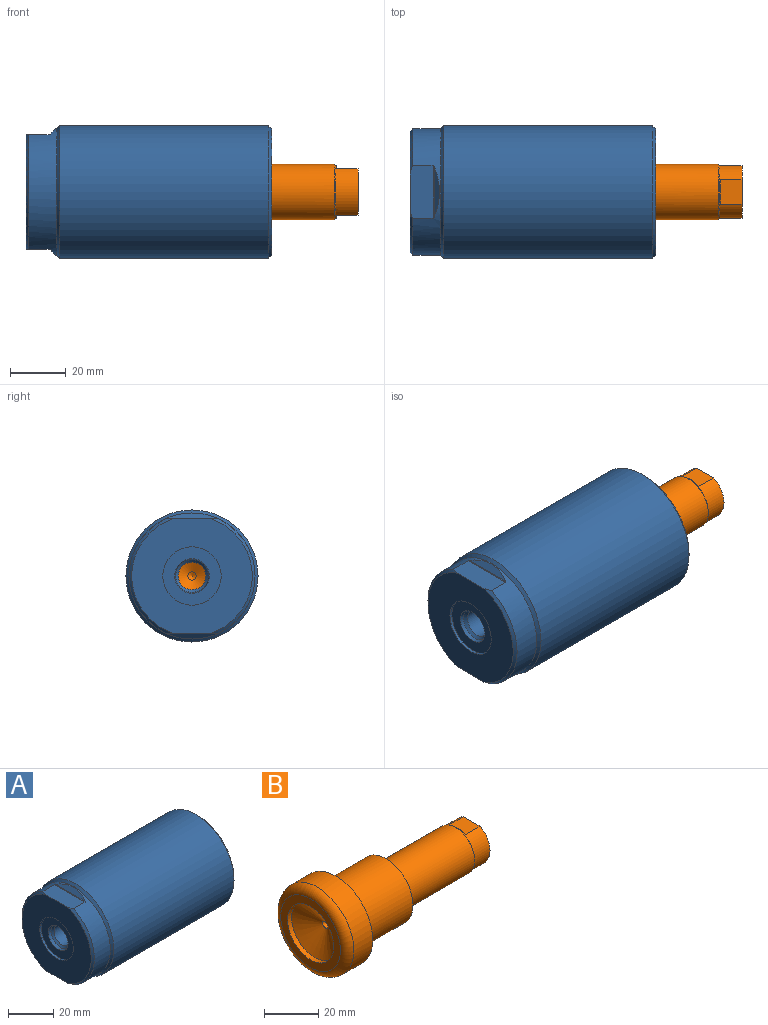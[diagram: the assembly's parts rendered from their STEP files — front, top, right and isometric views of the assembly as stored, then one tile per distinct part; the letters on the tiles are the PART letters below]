
ASSEMBLY  parts=2 mates=1
PART A: 32 faces, bbox 88.6x47.7x47.7 mm
  f0: cone r=0mm half-angle=45deg, axis (1,0,0), area 46mm2, adj f1,f2
  f1: plane 19.8x19.8mm, normal (1,0,0), area 198.7mm2, adj f0,f3
  f2: cylinder r=4.94mm len=9.88mm, axis (1,0,0), area 258.5mm2, adj f0,f4
  f3: cone r=0mm half-angle=45deg, axis (-1,0,0), area 152.1mm2, adj f1,f5
  f4: cone r=0mm half-angle=45deg, axis (-1,0,0), area 46mm2, adj f2,f6
  f5: plane 32.13x32.13mm, normal (1,0,0), area 395.3mm2, adj f3,f7
  f6: cone r=0mm half-angle=12deg, axis (-1,0,0), area 52.9mm2, adj f4,f8
  f7: torus R=16.06mm, axis (1,0,0), area 532.2mm2, adj f5,f9
  f8: plane 21.03x21.03mm, normal (-1,0,0), area 227.2mm2, adj f6,f10
  f9: cylinder r=19.06mm len=60.4mm, axis (1,0,0), area 7235.3mm2, adj f7,f11
  f10: cylinder r=10.52mm len=21.03mm, axis (1,0,0), area 66.1mm2, adj f8,f12
  f11: cone r=0mm half-angle=15deg, axis (1,0,0), area 315.5mm2, adj f9,f13
  f12: plane 43.4x41.2mm, normal (-1,0,0), area 1111.8mm2, adj f10,f15,f19,f20,f21
  f13: plane 40.1x40.1mm, normal (1,0,0), area 39.4mm2, adj f11,f22
  f14: plane 18.43x1.95mm, normal (-0.71,0,-0.71), area 34.2mm2, adj f16,f23
  f15: plane 19.19x8.41mm, normal (0,0,-1), area 155.6mm2, adj f12,f16,f20,f21,f23
  f16: cylinder r=0.5mm len=19.07mm, axis (0,-1,0), area 7.4mm2, adj f14,f15,f23
  f17: plane 18.43x1.95mm, normal (-0.71,0,0.71), area 34.2mm2, adj f18,f23
  f18: cylinder r=0.5mm len=19.07mm, axis (0,-1,0), area 7.4mm2, adj f17,f19,f23
  f19: plane 19.19x8.41mm, normal (0,0,1), area 155.6mm2, adj f12,f18,f20,f21,f23
  f20: cone r=0mm half-angle=45deg, axis (1,0,0), area 75mm2, adj f12,f15,f19,f23
  f21: cone r=0mm half-angle=45deg, axis (1,0,0), area 75mm2, adj f12,f15,f19,f23
  f22: torus R=20.05mm, axis (1,0,0), area 204.2mm2, adj f13,f24
  f23: cylinder r=22.7mm len=45.4mm, axis (-1,0,0), area 1076.3mm2, adj f14,f15,f16,f17,f18,f19,f20,f21
  f24: cylinder r=21.05mm len=42.1mm, axis (1,0,0), area 132.3mm2, adj f22,f26
  f25: cone r=0mm half-angle=45deg, axis (1,0,0), area 225.1mm2, adj f23,f27
  f26: cone r=0mm half-angle=45deg, axis (-1,0,0), area 157.9mm2, adj f24,f28
  f27: cylinder r=23.79mm len=75.41mm, axis (-1,0,0), area 11272.1mm2, adj f25,f29
  f28: cylinder r=20.19mm len=40.38mm, axis (-1,0,0), area 999mm2, adj f26,f30
  f29: cone r=0mm half-angle=45deg, axis (-1,0,0), area 206.9mm2, adj f27,f31
  f30: cone r=0mm half-angle=45deg, axis (1,0,0), area 157.9mm2, adj f28,f31
  f31: plane 45.58x45.58mm, normal (1,0,0), area 239.6mm2, adj f29,f30
PART B: 22 faces, bbox 83.8x41.2x41.2 mm
  f0: cone r=0mm half-angle=62deg, axis (-1,0,0), area 8mm2, adj f1
  f1: cylinder r=1.5mm len=3mm, axis (1,0,0), area 28.3mm2, adj f0,f2
  f2: cone r=0mm half-angle=62deg, axis (-1,0,0), area 504.4mm2, adj f1,f3
  f3: cylinder r=12mm len=24mm, axis (1,0,0), area 158.3mm2, adj f2,f4
  f4: plane 31.02x31.02mm, normal (-1,0,0), area 303.3mm2, adj f3,f5
  f5: torus R=15.51mm, axis (1,0,0), area 612.7mm2, adj f4,f6
  f6: cylinder r=19.01mm len=38.02mm, axis (1,0,0), area 1170.5mm2, adj f5,f7
  f7: plane 38.02x38.02mm, normal (1,0,0), area 479.3mm2, adj f6,f8
  f8: torus R=14.45mm, axis (1,0,0), area 69.7mm2, adj f7,f9
  f9: cylinder r=13.95mm len=27.9mm, axis (1,0,0), area 2235.1mm2, adj f8,f10
  f10: plane 27.9x27.9mm, normal (1,0,0), area 274.8mm2, adj f9,f11
  f11: torus R=10.35mm, axis (1,0,0), area 39.9mm2, adj f10,f12
  f12: cylinder r=9.95mm len=35.65mm, axis (1,0,0), area 2228.8mm2, adj f11,f15
  f13: plane 8.68x1.05mm, normal (1,0,0), area 6.1mm2, adj f18,f19
  f14: plane 8.68x1.05mm, normal (1,0,0), area 6.1mm2, adj f17,f19
  f15: cone r=0mm half-angle=45deg, axis (-1,0,0), area 38.9mm2, adj f12,f19
  f16: cone r=0mm half-angle=59deg, axis (1,0,0), area 104.9mm2, adj f20
  f17: plane 8.68x7.7mm, normal (0,0,-1), area 66.9mm2, adj f14,f19,f21
  f18: plane 8.68x7.7mm, normal (0,0,1), area 66.9mm2, adj f13,f19,f21
  f19: cylinder r=9.5mm len=19mm, axis (1,0,0), area 338.7mm2, adj f13,f14,f15,f17,f18,f21
  f20: cylinder r=5.35mm len=18mm, axis (1,0,0), area 605.1mm2, adj f16,f21
  f21: plane 19x16.9mm, normal (1,0,0), area 181.3mm2, adj f17,f18,f19,f20
PLACE A t=(28.84,7.21,-12.6)mm fixed
PLACE B rot(axis=(1,0,0),0deg) t=(27.04,7.21,-12.6)mm
MATE cylindrical A.f0 <-> B.f0  axis (1,0,0) through (28.79,7.21,-12.6)mm
